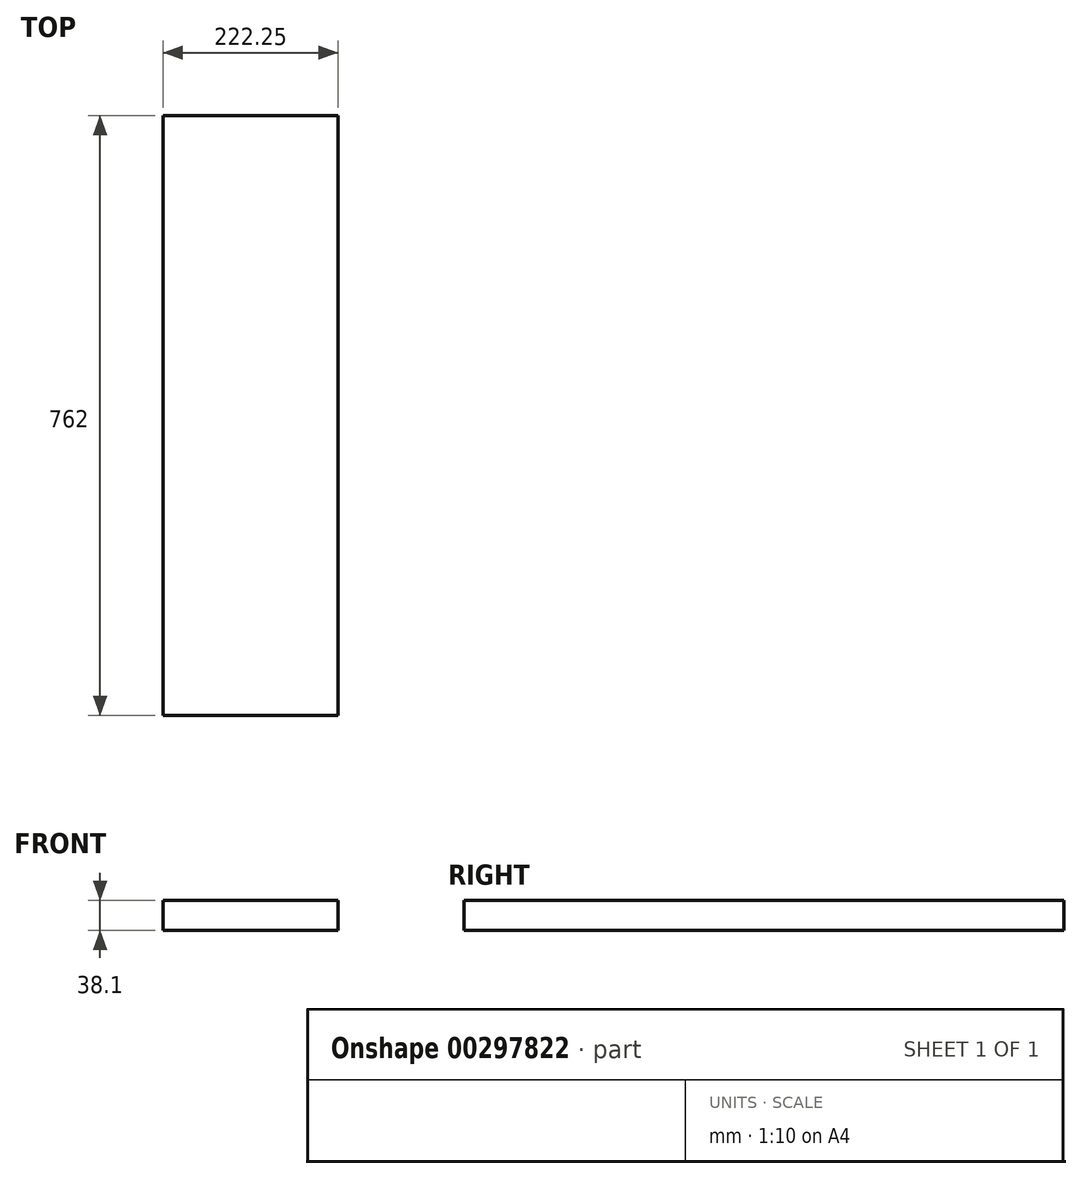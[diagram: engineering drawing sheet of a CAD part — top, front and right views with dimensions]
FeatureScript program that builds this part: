
annotation { "Feature Type Name" : "Feature", "Feature Type Description" : "" }
export const myFeature = defineFeature(function(context is Context, id is Id, definition is map)
    precondition{}
    {
        {
            var Q0;
            Q0=qCreatedBy(makeId("Top.planeOp"),FACE);
            var sketch = newSketch(context, id + "F0", { "sketchPlane" : qUnion([Q0])});
            skLineSegment(sketch, "E0.bottom", {"start": v(0, 0) * mm, "end": v(222.25, 0) * mm});
            skLineSegment(sketch, "E0.top", {"start": v(0, 762) * mm, "end": v(222.25, 762) * mm});
            skLineSegment(sketch, "E0.left", {"start": v(0, 0) * mm, "end": v(0, 762) * mm});
            skLineSegment(sketch, "E0.right", {"start": v(222.25, 0) * mm, "end": v(222.25, 762) * mm});
            skSolve(sketch);
        }
        {
            var Q0;
            Q0=makeQuery(id+"F0.imprint","IMPRINT",FACE,{"disambiguationData":[TD([[makeQuery(id+"F0.imprint","IMPRINT",EDGE,{"derivedFrom":sQuery(id+"F0.wireOp",EDGE,"E0.bottom")}),1.0]])]});
            extrude(context, id + "F1", {"entities" : qUnion([Q0]), "depth" : 38.1 * mm});
        }
    });
